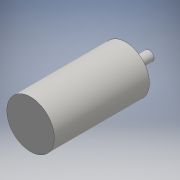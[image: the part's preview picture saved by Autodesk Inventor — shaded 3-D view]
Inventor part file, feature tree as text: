
AUTODESK INVENTOR PART (.ipt)
format: ipt  version: 2016 (Build 200138000, 138)  size: 96,256 bytes
history: native  units: mm
features: extrude x2, sketch x2, other x1
ambient origin geometry x8: Origin, YZ Plane, XZ Plane, XY Plane, X Axis, Y Axis, Z Axis, Center Point
bodies: Body1 (feature_tree)
feature tree (5):
  other  "ソリッド1"
  extrude  "押し出し1"  Depth=10.0mm
  extrude  "押し出し2"  Depth=20.0mm TaperAngle=0.0deg
  sketch  "スケッチ1"
  sketch  "スケッチ2"
